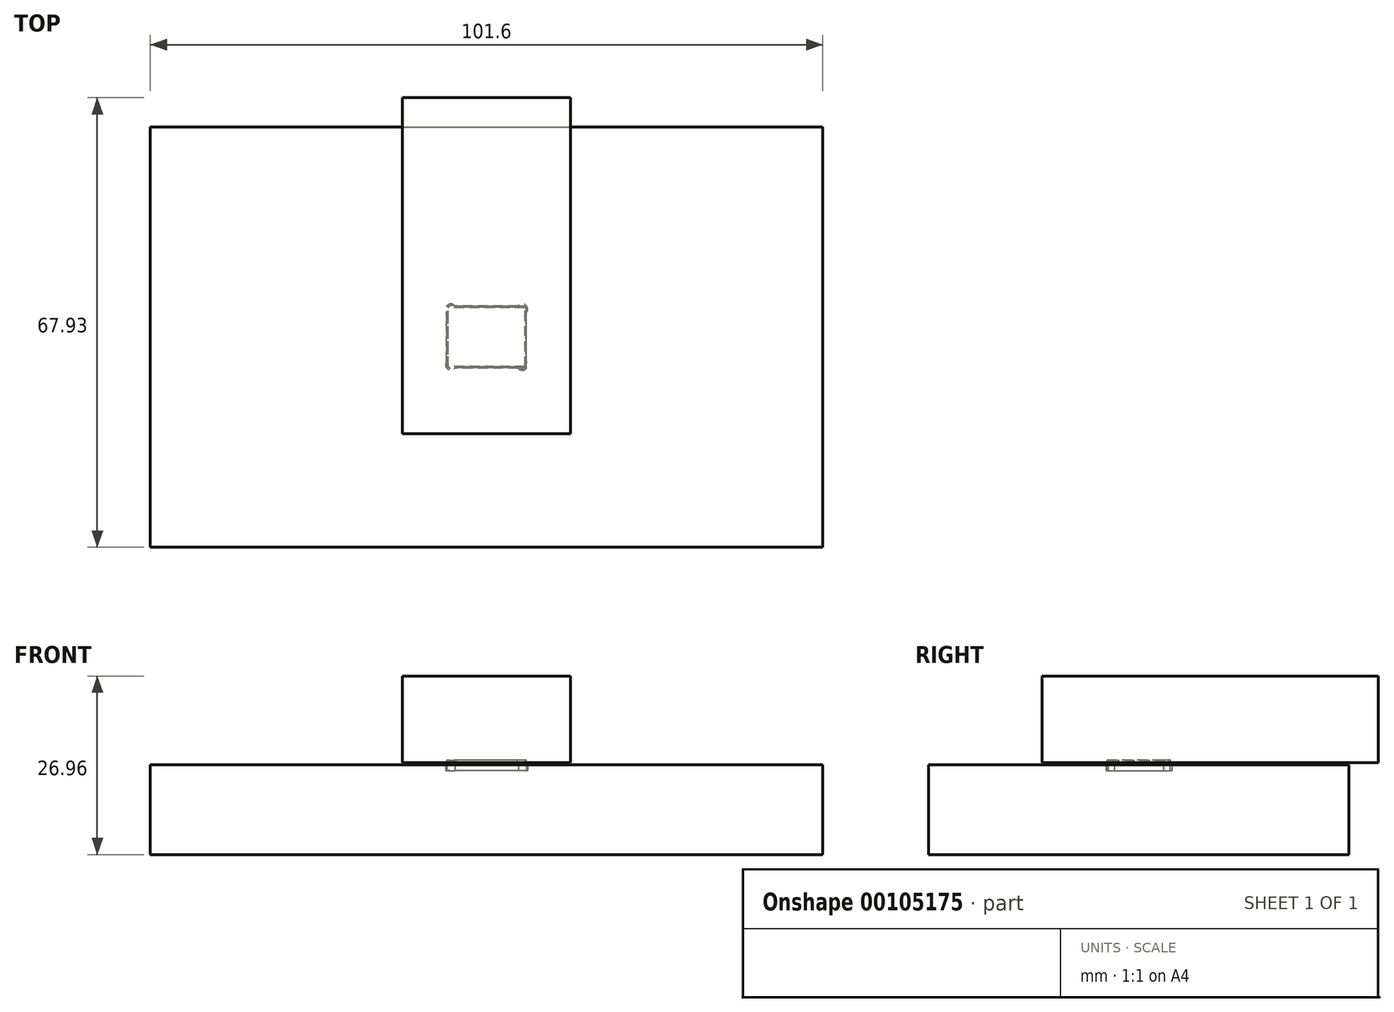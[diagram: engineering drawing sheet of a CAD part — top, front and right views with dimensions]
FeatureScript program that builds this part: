
annotation { "Feature Type Name" : "Feature", "Feature Type Description" : "" }
export const myFeature = defineFeature(function(context is Context, id is Id, definition is map)
    precondition{}
    {
        {
            var Q0;
            Q0=qCreatedBy(makeId("Top.planeOp"),FACE);
            var sketch = newSketch(context, id + "F0", { "sketchPlane" : qUnion([Q0])});
            skLineSegment(sketch, "E0.bottom", {"start": v(5.98, -4.65) * mm, "end": v(-5.98, -4.65) * mm});
            skLineSegment(sketch, "E0.top", {"start": v(5.98, 4.65) * mm, "end": v(-5.98, 4.65) * mm});
            skLineSegment(sketch, "E0.left", {"start": v(5.98, -4.65) * mm, "end": v(5.98, 4.65) * mm});
            skLineSegment(sketch, "E0.right", {"start": v(-5.98, -4.65) * mm, "end": v(-5.98, 4.65) * mm});
            skPoint(sketch, "E0.middle", {"position": v(0, 0) * mm});
            skSolve(sketch);
        }
        {
            var Q0;
            Q0=makeQuery(id+"F0.imprint","IMPRINT",FACE,{"disambiguationData":[TD([[makeQuery(id+"F0.imprint","IMPRINT",EDGE,{"derivedFrom":sQuery(id+"F0.wireOp",EDGE,"E0.bottom")}),-1.0]])]});
            extrude(context, id + "F1", {"entities" : qUnion([Q0]), "depth" : 1.08 * mm});
        }
        {
            var Q0;
            Q0=makeQuery(id+"F1.opExtrude","CAP_FACE",FACE,{"disambiguationData":[OSD([sQuery(id+"F0.wireOp",EDGE,"E0.bottom"),sQuery(id+"F0.wireOp",EDGE,"E0.top"),sQuery(id+"F0.wireOp",EDGE,"E0.left"),sQuery(id+"F0.wireOp",EDGE,"E0.right")])],"isStart":false});
            var sketch = newSketch(context, id + "F2", { "sketchPlane" : qUnion([Q0])});
            skLineSegment(sketch, "E1.0.0", {"start": v(-5.98, -4.65) * mm, "end": v(5.98, -4.65) * mm});
            skLineSegment(sketch, "E1.0.1", {"start": v(5.98, -4.65) * mm, "end": v(5.98, 4.65) * mm});
            skLineSegment(sketch, "E1.0.2", {"start": v(5.98, 4.65) * mm, "end": v(-5.98, 4.65) * mm});
            skLineSegment(sketch, "E1.0.3", {"start": v(-5.98, 4.65) * mm, "end": v(-5.98, -4.65) * mm});
            skLineSegment(sketch, "E2.bottom", {"start": v(5.8, -4.43) * mm, "end": v(-5.8, -4.43) * mm});
            skLineSegment(sketch, "E2.top", {"start": v(5.8, 4.43) * mm, "end": v(-5.8, 4.43) * mm});
            skLineSegment(sketch, "E2.left", {"start": v(5.8, -4.43) * mm, "end": v(5.8, 4.43) * mm});
            skLineSegment(sketch, "E2.right", {"start": v(-5.8, -4.43) * mm, "end": v(-5.8, 4.43) * mm});
            skPoint(sketch, "E2.middle", {"position": v(0, 0) * mm});
            skSolve(sketch);
        }
        {
            var Q0;
            Q0=makeQuery(id+"F2.imprint","IMPRINT",FACE,{"disambiguationData":[TD([[makeQuery(id+"F2.imprint","IMPRINT",EDGE,{"derivedFrom":sQuery(id+"F2.wireOp",EDGE,"E2.bottom")}),-1.0]])]});
            extrude(context, id + "F3", {"entities" : qUnion([Q0]), "depth" : 0.48 * mm});
        }
        {
            var Q0;
            Q0=qCreatedBy(makeId("Top.planeOp"),FACE);
            var sketch = newSketch(context, id + "F4", { "sketchPlane" : qUnion([Q0])});
            skLineSegment(sketch, "E3.bottom", {"start": v(-50.8, -31.75) * mm, "end": v(50.8, -31.75) * mm});
            skLineSegment(sketch, "E3.top", {"start": v(-50.8, 31.75) * mm, "end": v(50.8, 31.75) * mm});
            skLineSegment(sketch, "E3.left", {"start": v(-50.8, -31.75) * mm, "end": v(-50.8, 31.75) * mm});
            skLineSegment(sketch, "E3.right", {"start": v(50.8, -31.75) * mm, "end": v(50.8, 31.75) * mm});
            skPoint(sketch, "E3.middle", {"position": v(0, 0) * mm});
            skSolve(sketch);
        }
        {
            var Q0;
            Q0=makeQuery(id+"F4.imprint","IMPRINT",FACE,{"disambiguationData":[TD([[makeQuery(id+"F4.imprint","IMPRINT",EDGE,{"derivedFrom":sQuery(id+"F4.wireOp",EDGE,"E3.bottom")}),1.0]])]});
            extrude(context, id + "F5", {"entities" : qUnion([Q0]), "oppositeDirection" : true, "depth" : 12.7 * mm});
        }
        {
            var Q0;
            Q0=makeQuery(id+"F5.opExtrude","CAP_FACE",FACE,{"disambiguationData":[OSD([sQuery(id+"F4.wireOp",EDGE,"E3.bottom"),sQuery(id+"F4.wireOp",EDGE,"E3.top"),sQuery(id+"F4.wireOp",EDGE,"E3.left"),sQuery(id+"F4.wireOp",EDGE,"E3.right")])],"isStart":true});
            var sketch = newSketch(context, id + "F6", { "sketchPlane" : qUnion([Q0])});
            skLineSegment(sketch, "E4.0.0", {"start": v(-5.98, -4.65) * mm, "end": v(5.98, -4.65) * mm});
            skLineSegment(sketch, "E4.0.1", {"start": v(5.98, -4.65) * mm, "end": v(5.98, 4.65) * mm});
            skLineSegment(sketch, "E4.0.2", {"start": v(5.98, 4.65) * mm, "end": v(-5.98, 4.65) * mm});
            skLineSegment(sketch, "E4.0.3", {"start": v(-5.98, 4.65) * mm, "end": v(-5.98, -4.65) * mm});
            skLineSegment(sketch, "E5.bottom", {"start": v(6.03, -4.7) * mm, "end": v(-6.03, -4.7) * mm});
            skLineSegment(sketch, "E5.top", {"start": v(6.03, 4.7) * mm, "end": v(-6.03, 4.7) * mm});
            skLineSegment(sketch, "E5.left", {"start": v(6.03, -4.7) * mm, "end": v(6.03, 4.7) * mm});
            skLineSegment(sketch, "E5.right", {"start": v(-6.03, -4.7) * mm, "end": v(-6.03, 4.7) * mm});
            skPoint(sketch, "E5.middle", {"position": v(0, 0) * mm});
            skArc(sketch, "E6", {"start": v(-4.78, 4.7) * mm, "mid": v(-5.9, 4.84) * mm, "end": v(-6.03, 3.72) * mm});
            skLineSegment(sketch, "E7", {"start": v(0, 0) * mm, "end": v(-6.03, 4.7) * mm, "construction": true});
            skLineSegment(sketch, "E8", {"start": v(0, 0) * mm, "end": v(6.03, 0) * mm, "construction": true});
            skLineSegment(sketch, "E9", {"start": v(0, 0) * mm, "end": v(0, 4.7) * mm, "construction": true});
            skArc(sketch, "E10.MirrorCS", {"start": v(4.78, 4.7) * mm, "mid": v(5.9, 4.84) * mm, "end": v(6.03, 3.72) * mm});
            skArc(sketch, "E11.MirrorCS", {"start": v(4.78, -4.7) * mm, "mid": v(5.9, -4.84) * mm, "end": v(6.03, -3.72) * mm});
            skArc(sketch, "E12.MirrorCS", {"start": v(-4.78, -4.7) * mm, "mid": v(-5.9, -4.84) * mm, "end": v(-6.03, -3.72) * mm});
            skSolve(sketch);
        }
        {
            var Q0;
            Q0=makeQuery(id+"F6.imprint","IMPRINT",FACE,{"disambiguationData":[TD([[makeQuery(id+"F6.imprint","IMPRINT",EDGE,{"derivedFrom":makeQuery(id+"F5.opExtrude","CAP_EDGE",EDGE,{"disambiguationData":[OSD([sQuery(id+"F4.wireOp",EDGE,"E3.bottom")])],"isStart":true})}),1.0]])]});
            extrude(context, id + "F7", {"entities" : qUnion([Q0]), "operationType" : NewBodyOperationType.ADD, "depth" : 0.89 * mm});
        }
        {
            var Q0;
            Q0=makeQuery(id+"F3.opExtrude","CAP_FACE",FACE,{"disambiguationData":[OSD([sQuery(id+"F2.wireOp",EDGE,"E2.bottom"),sQuery(id+"F2.wireOp",EDGE,"E2.top"),sQuery(id+"F2.wireOp",EDGE,"E2.left"),sQuery(id+"F2.wireOp",EDGE,"E2.right")])],"isStart":false});
            var sketch = newSketch(context, id + "F8", { "sketchPlane" : qUnion([Q0])});
            skLineSegment(sketch, "E13.bottom", {"start": v(-12.7, -14.62) * mm, "end": v(12.7, -14.62) * mm});
            skLineSegment(sketch, "E13.top", {"start": v(-12.7, 36.18) * mm, "end": v(12.7, 36.18) * mm});
            skLineSegment(sketch, "E13.left", {"start": v(-12.7, -14.62) * mm, "end": v(-12.7, 36.18) * mm});
            skLineSegment(sketch, "E13.right", {"start": v(12.7, -14.62) * mm, "end": v(12.7, 36.18) * mm});
            skPoint(sketch, "E14", {"position": v(0, -14.62) * mm});
            skLineSegment(sketch, "E15.0.0", {"start": v(-5.8, -4.43) * mm, "end": v(5.8, -4.43) * mm});
            skLineSegment(sketch, "E15.0.1", {"start": v(5.8, -4.43) * mm, "end": v(5.8, 4.43) * mm});
            skLineSegment(sketch, "E15.0.2", {"start": v(5.8, 4.43) * mm, "end": v(-5.8, 4.43) * mm});
            skLineSegment(sketch, "E15.0.3", {"start": v(-5.8, 4.43) * mm, "end": v(-5.8, -4.43) * mm});
            skSolve(sketch);
        }
        {
            var Q0;
            Q0=makeQuery(id+"F8.imprint","IMPRINT",FACE,{"disambiguationData":[TD([[makeQuery(id+"F8.imprint","IMPRINT",EDGE,{"derivedFrom":sQuery(id+"F8.wireOp",EDGE,"E13.bottom")}),1.0]])]});
            var Q1;
            Q1=makeQuery(id+"F8.imprint","IMPRINT",FACE,{"disambiguationData":[TD([[makeQuery(id+"F8.imprint","IMPRINT",EDGE,{"derivedFrom":sQuery(id+"F8.wireOp",EDGE,"E15.0.0")}),-1.0]])]});
            extrude(context, id + "F9", {"entities" : qUnion([Q0, Q1]), "depth" : 12.7 * mm});
        }
        {
            var Q0;
            Q0=makeQuery(id+"F9.opExtrude","CAP_FACE",FACE,{"disambiguationData":[OSD([sQuery(id+"F8.wireOp",EDGE,"E13.bottom"),sQuery(id+"F8.wireOp",EDGE,"E13.top"),sQuery(id+"F8.wireOp",EDGE,"E13.left"),sQuery(id+"F8.wireOp",EDGE,"E13.right")])],"isStart":true});
            var sketch = newSketch(context, id + "F10", { "sketchPlane" : qUnion([Q0])});
            skLineSegment(sketch, "E16.0.0", {"start": v(5.8, 4.43) * mm, "end": v(-5.8, 4.43) * mm});
            skLineSegment(sketch, "E16.0.1", {"start": v(-5.8, 4.43) * mm, "end": v(-5.8, -4.43) * mm});
            skLineSegment(sketch, "E16.0.2", {"start": v(-5.8, -4.43) * mm, "end": v(5.8, -4.43) * mm});
            skLineSegment(sketch, "E16.0.3", {"start": v(5.8, -4.43) * mm, "end": v(5.8, 4.43) * mm});
            skLineSegment(sketch, "E17.bottom", {"start": v(5.85, -4.48) * mm, "end": v(-5.85, -4.48) * mm});
            skLineSegment(sketch, "E17.top", {"start": v(5.85, 4.48) * mm, "end": v(-5.85, 4.48) * mm});
            skLineSegment(sketch, "E17.left", {"start": v(5.85, -4.48) * mm, "end": v(5.85, 4.48) * mm});
            skLineSegment(sketch, "E17.right", {"start": v(-5.85, -4.48) * mm, "end": v(-5.85, 4.48) * mm});
            skPoint(sketch, "E17.middle", {"position": v(0, 0) * mm});
            skArc(sketch, "E18", {"start": v(-4.6, 4.48) * mm, "mid": v(-5.7, 4.63) * mm, "end": v(-5.85, 3.52) * mm});
            skLineSegment(sketch, "E19", {"start": v(0, 0) * mm, "end": v(-5.85, 4.48) * mm, "construction": true});
            skLineSegment(sketch, "E20", {"start": v(0, 0) * mm, "end": v(0, 4.43) * mm, "construction": true});
            skLineSegment(sketch, "E21", {"start": v(0, 0) * mm, "end": v(5.85, 0) * mm, "construction": true});
            skArc(sketch, "E22.MirrorCS", {"start": v(4.6, 4.48) * mm, "mid": v(5.7, 4.63) * mm, "end": v(5.85, 3.52) * mm});
            skArc(sketch, "E23.MirrorCS", {"start": v(4.6, -4.48) * mm, "mid": v(5.7, -4.63) * mm, "end": v(5.85, -3.52) * mm});
            skArc(sketch, "E24.MirrorCS", {"start": v(-4.6, -4.48) * mm, "mid": v(-5.7, -4.63) * mm, "end": v(-5.85, -3.52) * mm});
            skSolve(sketch);
        }
        {
            var Q0;
            Q0=makeQuery(id+"F10.imprint","IMPRINT",FACE,{"disambiguationData":[TD([[makeQuery(id+"F10.imprint","IMPRINT",EDGE,{"derivedFrom":makeQuery(id+"F9.opExtrude","CAP_EDGE",EDGE,{"disambiguationData":[OSD([sQuery(id+"F8.wireOp",EDGE,"E13.bottom")])],"isStart":true})}),-1.0]])]});
            extrude(context, id + "F11", {"entities" : qUnion([Q0]), "operationType" : NewBodyOperationType.ADD, "depth" : 0.36 * mm});
        }
    });
